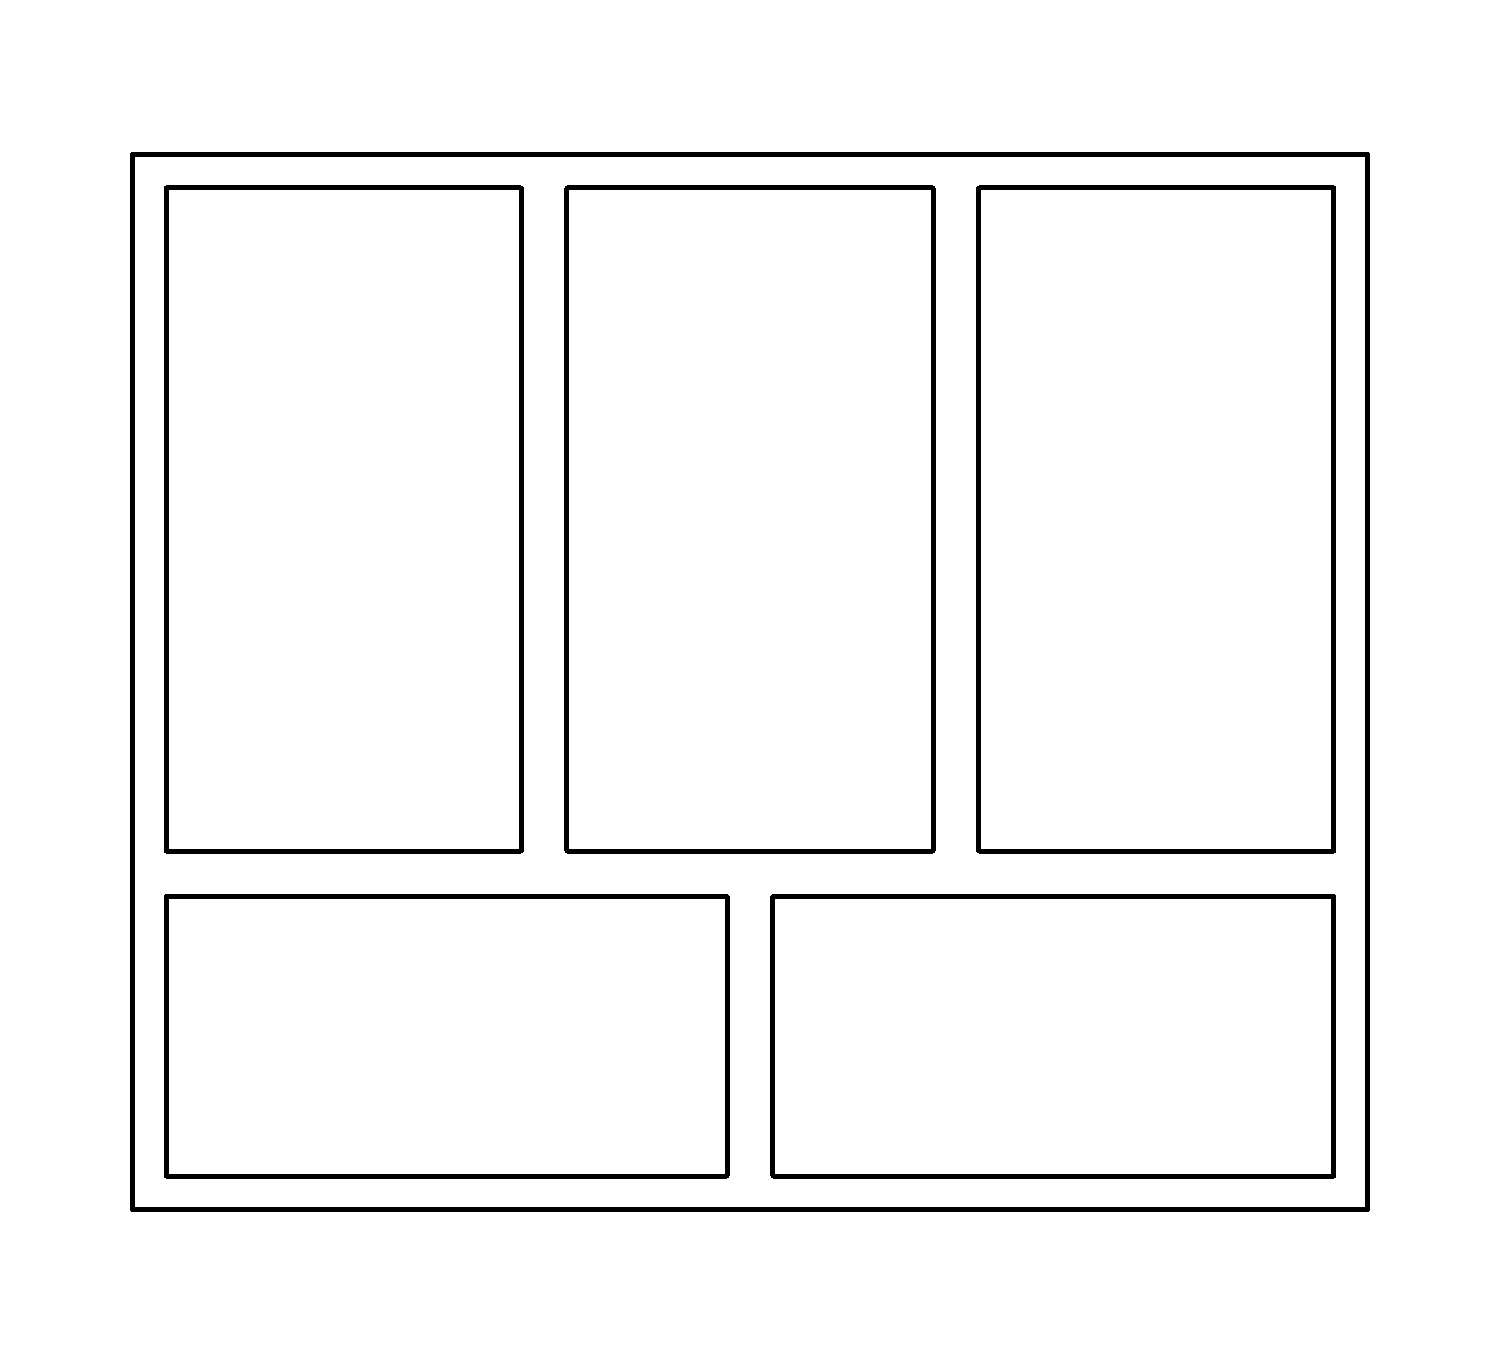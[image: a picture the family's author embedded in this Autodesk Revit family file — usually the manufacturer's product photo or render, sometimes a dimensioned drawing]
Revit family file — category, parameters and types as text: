
# Revit family: окна.rehau_трехпольное_2_фрамуги_снизу
name_source: partatom
category: Окна
revit_build: Autodesk Revit 2017 (Build: 20171027_0315(x64)
units: mm (PartAtom-declared; Revit-internal decimal feet)

## family parameters
Всегда вертикально = Да
Заголовок OmniClass = Windows
Номер OmniClass = 23.30.20.00
Общий = Нет
Основа = Стена
При загрузке вырезать с полостями = Нет
Точка расчета площади = Нет

## types (2) — shared parameters
24_мм = 24мм 1-камерный
32_мм = 32мм 2-камерный
40_мм = 40мм 2-камерный
42_мм = 42мм 2-камерный
50_мм = 50мм 2-камерный
60_blitz_new = 60 BLITZ NEW
60_euro_64 = 60 EURO (коробка 64, импост 78, створка 60)
60_euro_68 = 60 EURO (коробка 68, импост 78, створка 60)
60_euro_76 = 60 EURO (коробка 76, импост 86, створка 74)
70_delight_78 = 70 DELIGHT
70_grazio_55 = 70 GRAZIO (коробка 55)
70_grazio_63 = 70 GRAZIO (коробка 63)
80_intelio_58r = 80 INTELIO (коробка 58, створка R57)
80_intelio_58z = 80 INTELIO (коробка 58, створка Z57)
80_intelio_65r = 80 INTELIO (коробка 65, створка R57)
80_intelio_65z = 80 INTELIO (коробка 65, створка Z57)
ADSK_Обозначение = ГОСТ 30674-99
URL = https://www.rehau.com
sp_energy = Энергосберегающие стекла
sp_gaz = Заполненный газом
sp_standart = Обычный стеклопакет
sp_triplex = Триплекс
Аналитическая конструкция = Окна с одинарным остеклением - для жилых зданий
Высота подоконника по умолчанию = 900 мм
Высота створок = 1200 мм
Группа модели = ОП
Замыкание стены = По основе
Изготовитель = Rehau
Изображение типоразмера = схема_трехпольное_2_фрамуги_снизу.png
Коэффициент теплопередачи (U) = 5.7361 Вт/(м²·K)
Коэффициент теплопритока от солнечного излучения = 0.86
Материал коробки = <По категории>
Материал отлива = <По категории>
Материал подоконника = <По категории>
Материал стекла = <По категории>
Описание = проем.окно
Примерная высота = 1760 мм
Примерная ширина = 2060 мм
Пропускание видимого света = 0.9
Равные створки = Да
Створка слева = 400 мм
Створка справа = 400 мм
Термостойкость = 0.1743 (м²·K)/Вт
Тип створки центр = створка : глухая
Тип фрамуги слева = створка : глухая
Тип фрамуги справа = створка : глухая
глухая_створка = створка : глухая
обозначение_проема_высота = 293 мм
обозначение_проема_ширина = 343 мм
таблица выбора = каталог профилей Rehau

## per-type parameters (varying)
| type | Тип створки слева | Тип створки справа |
| 2060х1760 (2 створки и глухое) | створка : левая-откидная | створка : правая-откидная |
| 2060х1760 (глухое) | створка : глухая | створка : глухая |
